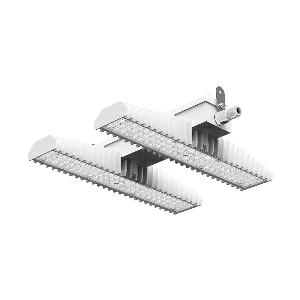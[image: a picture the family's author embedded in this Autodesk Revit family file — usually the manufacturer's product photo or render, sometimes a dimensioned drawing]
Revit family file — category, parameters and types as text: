
# Revit family: 3f_filippi_-_3f_lem_ho_concentrato_3f_filippi_-_58960_-_3f_lem_2_ho_led_140_cr_conc
name_source: partatom
category: Lighting Fixtures
units: mm (PartAtom-declared; Revit-internal decimal feet)

## family parameters
Cut with Voids When Loaded = No
Host = Face
Light Source = No
Part Type = Normal
Room Calculation Point = No
Round Connector Dimension = Use Diameter
Shared = No

## types (1)
- 3F Filippi - 3F LEM HO Concentrato (1 x LED, 21649 lm, 138 W, 4000 K)
    Apparent Load = 138 VA
    Approval mark = CE
    CIE Flux Codes = 83 96 99 100 100
    Color Rendering = 80
    Color Temperature = 4000 K
    Control Gear = Electronic ballast
    Default Elevation = 1800 mm
    Description = Industrial luminaire with high light output and high luminous efficiency designed with the most innovative technologies for environments with temperature up to 55°C.

ILLUMINOTECHNICAL
Luminous efficiency 100% (DLOR 100%, ULOR 0%).
Initial luminous flux of the luminaire 21649 lm.
Direct symmetric narrow distribution: the illuminated area has a elliptical shape.
Installation Interdistance Transv.D = 0.52 x hu - Long.D = 1.16 x hu.
Tabular UGR (CIE 117 - 4H-8H; S=0.25H; 70/50/20): RUG 17.8 - 21.6.
Beam angle: 31° - 73°.
Luminous efficacy 157 lm/W.
Lifetime (L93/B10): 30000 h. (tq+25°C)
Lifetime (L90/B10): 50000 h. (tq+25°C)
Lifetime (L85/B10): 80000 h. (tq+25°C)
Lifetime (L80/B10): 100000 h. (tq+25°C)
Lifetime (L85/B10): 50000 h. (tq+55°C)
Sudden decreased luminous flux after 50000 hours: 0% (C0).
Photobiological safety in compliance with IEC/TR 62778: RG0 risk exempt, (IEC 62471).
In compliance with IEC/EN 62722-2-1 - IEC/EN 62717 standards.

SOURCE
2 Mid-Power linear LED modules 70W/840.
Energy efficiency class (UE 2019/2020 - UE 2019/2015): C.
CIE 13.3 Colour rendering index: CRI >80 (R9 <50%).
IES TM-30 Fidelity Index: Rf = 84 Rg = 95.
CCT nominal colour temperature 4000 K.
Colour initial tolerance (MacAdam): SDCM 3.

MECHANICAL
Passive modular heatsinks in die-casted aluminium, painted in white colour.
To optimize the thermal management of the LED module, the heatsinks are oversized and provided with self-cleaning of cooling fins.
Wiring body in aluminium and galvanised steel anchored solidly to the sinks and thermally separated.
3F Lens lenses with high luminous efficiency, transparent methacrylate (PMMA), fixed to the LED modules.
Fixing brackets in stainless steel.
Luminaire with limited surface temperature. - D - (EN 60598-2-24)
Dimensions: 470x542 mm, height 129 mm. Weight 9.06 kg.
IP65 protection degree.
Mechanical strength to impacts IK06 (1 joule).
Glow-wire test resistance 650°C.

ELECTRICAL
Halogen Free electronic wiring 230V-50/60Hz, power factor 0.97, THD <25%, constant output current, class I, 1 driver.
Power of the luminaire 138 W.
ENEC - CE.
SAFE FLICKER: PstLM=<1 and SVM=<0.4 (IEC TR 61547-1 and IEC TR 63158), to ensure a more comfortable and safe light.
Luminaire compliant with EN 60598-2-22 for power supply from a centralised emergency system CPSS (Central Power Supply System), not incorporated in the luminaire - high risk areas excluded. The default power and flux are 100% in AC and 100% in DC.
Ambient temperature from -30°C to +55°C.
Temperature class T6 max 85°C.
Quick connection via M20 3P connector with 9-13 mm tightening range.
Power unit positioned on a separate compartment by the LED module to ensure optimum temperatures of cabling components, to be inspectable and maintainable.
Relative humidity UR: <85%.

INSTALLATION
Ceiling / Suspended / Wall.
All accessories dedicated to this product are available on the Catalog and on our website www.3F-Filippi.com.

APPLICATIONS
In commercial environments, exhibition and industrial areas, stores, open areas or with shelves.
Environments in which it is necessary a total protection against falling fragments (eg environments with foodstuffs or machines with moving parts or with extreme temperature changes), use luminaires with polycarbonate lenses.

WARNING
Fixture not suitable for cold stores with an ambient temperature <0°C and/or relative humidity >85%.
Luminaire designed for disposal/recycling at end-of-life.
Replaceable (LED only) light source by a professional. Replaceable control gear by a professional.
    Height = 129 mm
    Lamp = 1 x LED
    Lamp Light Flux = 21649 lm
    Lamp Power = 138 W
    Lamp count = 1
    Length = 470 mm
    Lifetime = 50000 h
    Luminous efficacy = 157 lm/W
    Manufacturer = 3F Filippi
    ModVariant = No
    Model = 3F Filippi - 58960 - 3F LEM 2 HO LED 140 CR CONC
    Mounting Place = Ceiling
    Mounting Type = Pendant
    Number of Poles = 1
    OnlyDefault = Yes
    Power Factor = 1
    Product Name = 3F Filippi - 3F LEM HO Concentrato
    Product group = pendant luminaire
    ProductGroupID = 9
    Protection Class = Protection class I
    Protection Degree = IP 65
    RLX_Detail_Level = 1
    RLX_Emergency_Light_Flux = 0 lm
    RLX_Emergency_Type = 0
    RLX_Emergency_Type_DB = No
    RlxData = <blob elided: 96565 chars, md5=86b32e9d>
    Socket = socket
    Standby Power = 0 W
    System Light Flux = 21649 lm
    System Power = 138 W
    Type Comments = Product without accessories
    Type Image = 3f_filippi_-_lem_2.jpg
    URL = http://relux.com
    VarID = ---
    Voltage = 0 V
    Weight = 0.00 kg
    Width = 542 mm

## geometry (parser evidence)
native form markers: Blend x4, Sweep x11
no freeform markers — native parametric forms only
